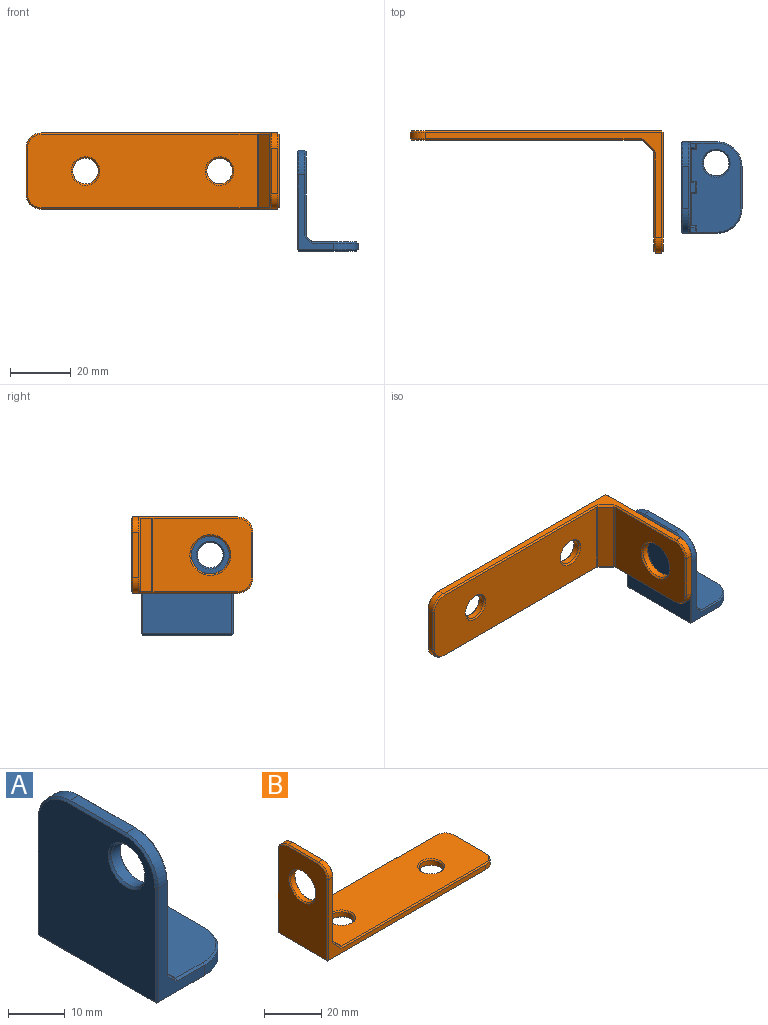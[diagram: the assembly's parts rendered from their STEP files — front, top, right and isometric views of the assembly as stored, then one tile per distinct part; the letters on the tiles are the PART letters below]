
ASSEMBLY  parts=2 mates=1
PART A: 74 faces, bbox 20x30x33 mm
  f0: plane 29.2x16.2mm, normal (0,0,1), area 368mm2, adj f21,f24,f25,f28,f29,f34,f37,f40
  f1: plane 29.2x29.2mm, normal (1,0,0), area 747.6mm2, adj f21,f26,f27,f30,f31,f35,f39,f41
  f2: plane 32.2x29.2mm, normal (-1,0,0), area 849mm2, adj f59,f60,f61,f64,f66,f67,f73
  f3: plane 29.2x19.2mm, normal (0,0,-1), area 469.4mm2, adj f62,f65,f66,f68,f70,f71,f72
  f4: plane 14x2.2mm, normal (1,0,0), area 30.8mm2, adj f13,f15,f43,f68
  f5: plane 14x2.2mm, normal (0,0,1), area 30.8mm2, adj f14,f16,f45,f61
  f6: plane 24.6x11.6mm, normal (0,-1,0), area 77.4mm2, adj f15,f16,f32,f33,f36,f37,f39,f67
  f7: plane 24.6x11.6mm, normal (0,1,0), area 77.4mm2, adj f13,f14,f50,f53,f54,f55,f56,f60
  f8: cylinder r=4.2mm len=8.4mm, axis (0,0,1), area 58.1mm2, adj f57,f72
  f9: cylinder r=4.2mm len=8.4mm, axis (1,0,0), area 58.1mm2, adj f58,f73
  f10: plane 3.57x1.77mm, normal (0.71,0,0.71), area 7.7mm2, adj f11,f12,f25,f26,f29,f30,f34,f35
  f11: plane 1.2x1.2mm, normal (0,-1,0), area 0.7mm2, adj f10,f25,f26
  f12: plane 1.2x1.2mm, normal (0,1,0), area 0.7mm2, adj f10,f34,f35
  f13: cylinder r=8mm len=8mm, axis (0,0,1), area 27.6mm2, adj f4,f7,f46,f65
  f14: cylinder r=8mm len=8mm, axis (-1,0,0), area 27.6mm2, adj f5,f7,f49,f59
  f15: cylinder r=8mm len=8mm, axis (0,0,-1), area 27.6mm2, adj f4,f6,f40,f70
  f16: cylinder r=8mm len=8mm, axis (1,0,0), area 27.6mm2, adj f5,f6,f42,f64
  f17: plane 1.88x1.77mm, normal (0.71,0,0.71), area 4.1mm2, adj f18,f24,f27,f28,f31,f32
  f18: plane 1.2x1.2mm, normal (0,1,0), area 0.7mm2, adj f17,f24,f27
  f19: plane 1.88x1.77mm, normal (0.71,0,0.71), area 4.1mm2, adj f20,f47,f48,f51,f52,f56
  f20: plane 1.2x1.2mm, normal (0,-1,0), area 0.7mm2, adj f19,f47,f48
  f21: plane 10.7x0.4mm, normal (0.71,0,0.71), area 6.1mm2, adj f0,f1,f22,f23
  f22: plane 0.4x0.4mm, normal (0.58,-0.58,0.58), area 0.1mm2, adj f21,f25,f26
  f23: plane 0.4x0.4mm, normal (0.58,0.58,0.58), area 0.1mm2, adj f21,f24,f27
  f24: plane 1.77x0.4mm, normal (0,0.71,0.71), area 0.8mm2, adj f0,f17,f18,f23,f28
  f25: plane 1.77x0.4mm, normal (0,-0.71,0.71), area 0.8mm2, adj f0,f10,f11,f22,f29
  f26: plane 1.77x0.4mm, normal (0.71,-0.71,0), area 0.8mm2, adj f1,f10,f11,f22,f30
  f27: plane 1.77x0.4mm, normal (0.71,0.71,0), area 0.8mm2, adj f1,f17,f18,f23,f31
  f28: plane 2x0.28mm, normal (0.38,0,0.92), area 0.6mm2, adj f0,f17,f24,f33
  f29: plane 3.8x0.28mm, normal (0.38,0,0.92), area 1.1mm2, adj f0,f10,f25,f34
  f30: plane 3.8x0.28mm, normal (0.92,0,0.38), area 1.1mm2, adj f1,f10,f26,f35
  f31: plane 2x0.28mm, normal (0.92,0,0.38), area 0.6mm2, adj f1,f17,f27,f36
  f32: plane 2.05x2.05mm, normal (0.5,-0.71,0.5), area 1.4mm2, adj f6,f17,f33,f36
  f33: plane 0.57x0.52mm, normal (0.28,-0.68,0.68), area 0.3mm2, adj f6,f28,f32,f37
  f34: plane 1.77x0.4mm, normal (0,0.71,0.71), area 0.8mm2, adj f0,f10,f12,f29,f38
  f35: plane 1.77x0.4mm, normal (0.71,0.71,0), area 0.8mm2, adj f1,f10,f12,f30,f38
  f36: plane 0.57x0.52mm, normal (0.68,-0.68,0.28), area 0.3mm2, adj f6,f31,f32,f39
  f37: plane 6.83x0.4mm, normal (0,-0.71,0.71), area 3.9mm2, adj f0,f6,f33,f40
  f38: plane 0.4x0.4mm, normal (0.58,0.58,0.58), area 0.1mm2, adj f34,f35,f41
  f39: plane 19.83x0.4mm, normal (0.71,-0.71,0), area 11.2mm2, adj f1,f6,f36,f42
  f40: cone r=7.6mm half-angle=45deg, axis (0,0,-1), area 6.9mm2, adj f0,f15,f37,f43
  f41: plane 10.7x0.4mm, normal (0.71,0,0.71), area 6.1mm2, adj f0,f1,f38,f44
  f42: cone r=7.6mm half-angle=45deg, axis (-1,0,0), area 6.9mm2, adj f1,f16,f39,f45
  f43: plane 14x0.4mm, normal (0.71,0,0.71), area 7.9mm2, adj f0,f4,f40,f46
  f44: plane 0.4x0.4mm, normal (0.58,-0.58,0.58), area 0.1mm2, adj f41,f47,f48
  f45: plane 14x0.4mm, normal (0.71,0,0.71), area 7.9mm2, adj f1,f5,f42,f49
  f46: cone r=7.6mm half-angle=45deg, axis (0,0,-1), area 6.9mm2, adj f0,f13,f43,f50
  f47: plane 1.77x0.4mm, normal (0,-0.71,0.71), area 0.8mm2, adj f0,f19,f20,f44,f51
  f48: plane 1.77x0.4mm, normal (0.71,-0.71,0), area 0.8mm2, adj f1,f19,f20,f44,f52
  f49: cone r=7.6mm half-angle=45deg, axis (-1,0,0), area 6.9mm2, adj f1,f14,f45,f53
  f50: plane 6.83x0.4mm, normal (0,0.71,0.71), area 3.9mm2, adj f0,f7,f46,f54
  f51: plane 2x0.28mm, normal (0.38,0,0.92), area 0.6mm2, adj f0,f19,f47,f54
  f52: plane 2x0.28mm, normal (0.92,0,0.38), area 0.6mm2, adj f1,f19,f48,f55
  f53: plane 19.83x0.4mm, normal (0.71,0.71,0), area 11.2mm2, adj f1,f7,f49,f55
  f54: plane 0.57x0.52mm, normal (0.28,0.68,0.68), area 0.3mm2, adj f7,f50,f51,f56
  f55: plane 0.57x0.52mm, normal (0.68,0.68,0.28), area 0.3mm2, adj f7,f52,f53,f56
  f56: plane 2.05x2.05mm, normal (0.5,0.71,0.5), area 1.4mm2, adj f7,f19,f54,f55
  f57: cone r=4.2mm half-angle=45deg, axis (0,0,1), area 15.6mm2, adj f0,f8
  f58: cone r=4.2mm half-angle=45deg, axis (1,0,0), area 15.6mm2, adj f1,f9
  f59: cone r=7.6mm half-angle=45deg, axis (1,0,0), area 6.9mm2, adj f2,f14,f60,f61
  f60: plane 24.6x0.4mm, normal (-0.71,0.71,0), area 13.9mm2, adj f2,f7,f59,f63
  f61: plane 14x0.4mm, normal (-0.71,0,0.71), area 7.9mm2, adj f2,f5,f59,f64
  f62: plane 11.6x0.4mm, normal (0,0.71,-0.71), area 6.6mm2, adj f3,f7,f63,f65
  f63: plane 0.4x0.4mm, normal (-0.58,0.58,-0.58), area 0.1mm2, adj f60,f62,f66
  f64: cone r=7.6mm half-angle=45deg, axis (1,0,0), area 6.9mm2, adj f2,f16,f61,f67
  f65: cone r=7.6mm half-angle=45deg, axis (0,0,1), area 6.9mm2, adj f3,f13,f62,f68
  f66: plane 29.2x0.4mm, normal (-0.71,0,-0.71), area 16.5mm2, adj f2,f3,f63,f69
  f67: plane 24.6x0.4mm, normal (-0.71,-0.71,0), area 13.9mm2, adj f2,f6,f64,f69
  f68: plane 14x0.4mm, normal (0.71,0,-0.71), area 7.9mm2, adj f3,f4,f65,f70
  f69: plane 0.4x0.4mm, normal (-0.58,-0.58,-0.58), area 0.1mm2, adj f66,f67,f71
  f70: cone r=7.6mm half-angle=45deg, axis (0,0,1), area 6.9mm2, adj f3,f15,f68,f71
  f71: plane 11.6x0.4mm, normal (0,-0.71,-0.71), area 6.6mm2, adj f3,f6,f69,f70
  f72: cone r=4.6mm half-angle=45deg, axis (0,0,-1), area 15.6mm2, adj f3,f8
  f73: cone r=4.6mm half-angle=45deg, axis (-1,0,0), area 15.6mm2, adj f2,f9
PART B: 53 faces, bbox 83x25x40 mm
  f0: plane 75.29x24mm, normal (0,0,1), area 1659.5mm2, adj f17,f21,f22,f26,f29,f30,f51,f52
  f1: plane 32.29x24mm, normal (1,0,0), area 625.3mm2, adj f16,f18,f19,f23,f27,f28,f34
  f2: plane 39x24mm, normal (-1,0,0), area 786.3mm2, adj f38,f41,f43,f44,f46,f47,f48
  f3: plane 82x24mm, normal (0,0,-1), area 1820.5mm2, adj f35,f36,f37,f39,f42,f43,f49,f50
  f4: plane 15x2mm, normal (1,0,0), area 30mm2, adj f12,f14,f22,f36
  f5: plane 15x2mm, normal (0,0,1), area 30mm2, adj f13,f15,f18,f44
  f6: plane 77.5x34.5mm, normal (0,-1,0), area 229.3mm2, adj f14,f15,f27,f30,f31,f32,f33,f42
  f7: plane 77.5x34.5mm, normal (0,1,0), area 229.3mm2, adj f12,f13,f19,f20,f21,f24,f25,f37
  f8: cylinder r=6.2mm len=12.4mm, axis (-1,0,0), area 77.9mm2, adj f34,f48
  f9: cylinder r=4.2mm len=8.4mm, axis (0,0,-1), area 52.8mm2, adj f49,f51
  f10: cylinder r=4.2mm len=8.4mm, axis (0,0,-1), area 52.8mm2, adj f50,f52
  f11: plane 24x3.71mm, normal (0.71,0,0.71), area 125.8mm2, adj f20,f28,f29,f33
  f12: cylinder r=5mm len=5mm, axis (0,0,1), area 15.7mm2, adj f4,f7,f17,f35
  f13: cylinder r=5mm len=5mm, axis (-1,0,0), area 15.7mm2, adj f5,f7,f16,f41
  f14: cylinder r=5mm len=5mm, axis (0,0,-1), area 15.7mm2, adj f4,f6,f26,f39
  f15: cylinder r=5mm len=5mm, axis (1,0,0), area 15.7mm2, adj f5,f6,f23,f46
  f16: cone r=4.5mm half-angle=45deg, axis (-1,0,0), area 5.3mm2, adj f1,f13,f18,f19
  f17: cone r=4.5mm half-angle=45deg, axis (0,0,-1), area 5.3mm2, adj f0,f12,f21,f22
  f18: plane 15x0.5mm, normal (0.71,0,0.71), area 10.6mm2, adj f1,f5,f16,f23
  f19: plane 27.79x0.5mm, normal (0.71,0.71,0), area 19.7mm2, adj f1,f7,f16,f24
  f20: plane 4.06x4.06mm, normal (0.5,0.71,0.5), area 3.7mm2, adj f7,f11,f24,f25
  f21: plane 70.79x0.5mm, normal (0,0.71,0.71), area 50.1mm2, adj f0,f7,f17,f25
  f22: plane 15x0.5mm, normal (0.71,0,0.71), area 10.6mm2, adj f0,f4,f17,f26
  f23: cone r=4.5mm half-angle=45deg, axis (-1,0,0), area 5.3mm2, adj f1,f15,f18,f27
  f24: plane 0.71x0.65mm, normal (0.68,0.68,0.28), area 0.4mm2, adj f7,f19,f20,f28
  f25: plane 0.71x0.65mm, normal (0.28,0.68,0.68), area 0.4mm2, adj f7,f20,f21,f29
  f26: cone r=4.5mm half-angle=45deg, axis (0,0,-1), area 5.3mm2, adj f0,f14,f22,f30
  f27: plane 27.79x0.5mm, normal (0.71,-0.71,0), area 19.7mm2, adj f1,f6,f23,f31
  f28: plane 24x0.35mm, normal (0.92,0,0.38), area 9.2mm2, adj f1,f11,f24,f31
  f29: plane 24x0.35mm, normal (0.38,0,0.92), area 9.2mm2, adj f0,f11,f25,f32
  f30: plane 70.79x0.5mm, normal (0,-0.71,0.71), area 50.1mm2, adj f0,f6,f26,f32
  f31: plane 0.71x0.65mm, normal (0.68,-0.68,0.28), area 0.4mm2, adj f6,f27,f28,f33
  f32: plane 0.71x0.65mm, normal (0.28,-0.68,0.68), area 0.4mm2, adj f6,f29,f30,f33
  f33: plane 4.06x4.06mm, normal (0.5,-0.71,0.5), area 3.7mm2, adj f6,f11,f31,f32
  f34: cone r=6.2mm half-angle=45deg, axis (1,0,0), area 28.7mm2, adj f1,f8
  f35: cone r=4.5mm half-angle=45deg, axis (0,0,1), area 5.3mm2, adj f3,f12,f36,f37
  f36: plane 15x0.5mm, normal (0.71,0,-0.71), area 10.6mm2, adj f3,f4,f35,f39
  f37: plane 77.5x0.5mm, normal (0,0.71,-0.71), area 54.8mm2, adj f3,f7,f35,f40
  f38: plane 34.5x0.5mm, normal (-0.71,0.71,0), area 24.4mm2, adj f2,f7,f40,f41
  f39: cone r=4.5mm half-angle=45deg, axis (0,0,1), area 5.3mm2, adj f3,f14,f36,f42
  f40: plane 0.5x0.5mm, normal (-0.58,0.58,-0.58), area 0.2mm2, adj f37,f38,f43
  f41: cone r=4.5mm half-angle=45deg, axis (1,0,0), area 5.3mm2, adj f2,f13,f38,f44
  f42: plane 77.5x0.5mm, normal (0,-0.71,-0.71), area 54.8mm2, adj f3,f6,f39,f45
  f43: plane 24x0.5mm, normal (-0.71,0,-0.71), area 17mm2, adj f2,f3,f40,f45
  f44: plane 15x0.5mm, normal (-0.71,0,0.71), area 10.6mm2, adj f2,f5,f41,f46
  f45: plane 0.5x0.5mm, normal (-0.58,-0.58,-0.58), area 0.2mm2, adj f42,f43,f47
  f46: cone r=4.5mm half-angle=45deg, axis (1,0,0), area 5.3mm2, adj f2,f15,f44,f47
  f47: plane 34.5x0.5mm, normal (-0.71,-0.71,0), area 24.4mm2, adj f2,f6,f45,f46
  f48: cone r=6.2mm half-angle=45deg, axis (-1,0,0), area 28.7mm2, adj f2,f8
  f49: cone r=4.2mm half-angle=45deg, axis (0,0,-1), area 19.8mm2, adj f3,f9
  f50: cone r=4.2mm half-angle=45deg, axis (0,0,-1), area 19.8mm2, adj f3,f10
  f51: cone r=4.2mm half-angle=45deg, axis (0,0,1), area 19.8mm2, adj f0,f9
  f52: cone r=4.2mm half-angle=45deg, axis (0,0,1), area 19.8mm2, adj f0,f10
PLACE A t=(18.17,103.34,8.63)mm
PLACE B rot(axis=(0,0.71,-0.71),180deg) t=(12.27,106.84,22.38)mm
MATE cylindrical B.f8 <-> A.f9  axis (1,0,0) through (10.77,80.84,34.88)mm
